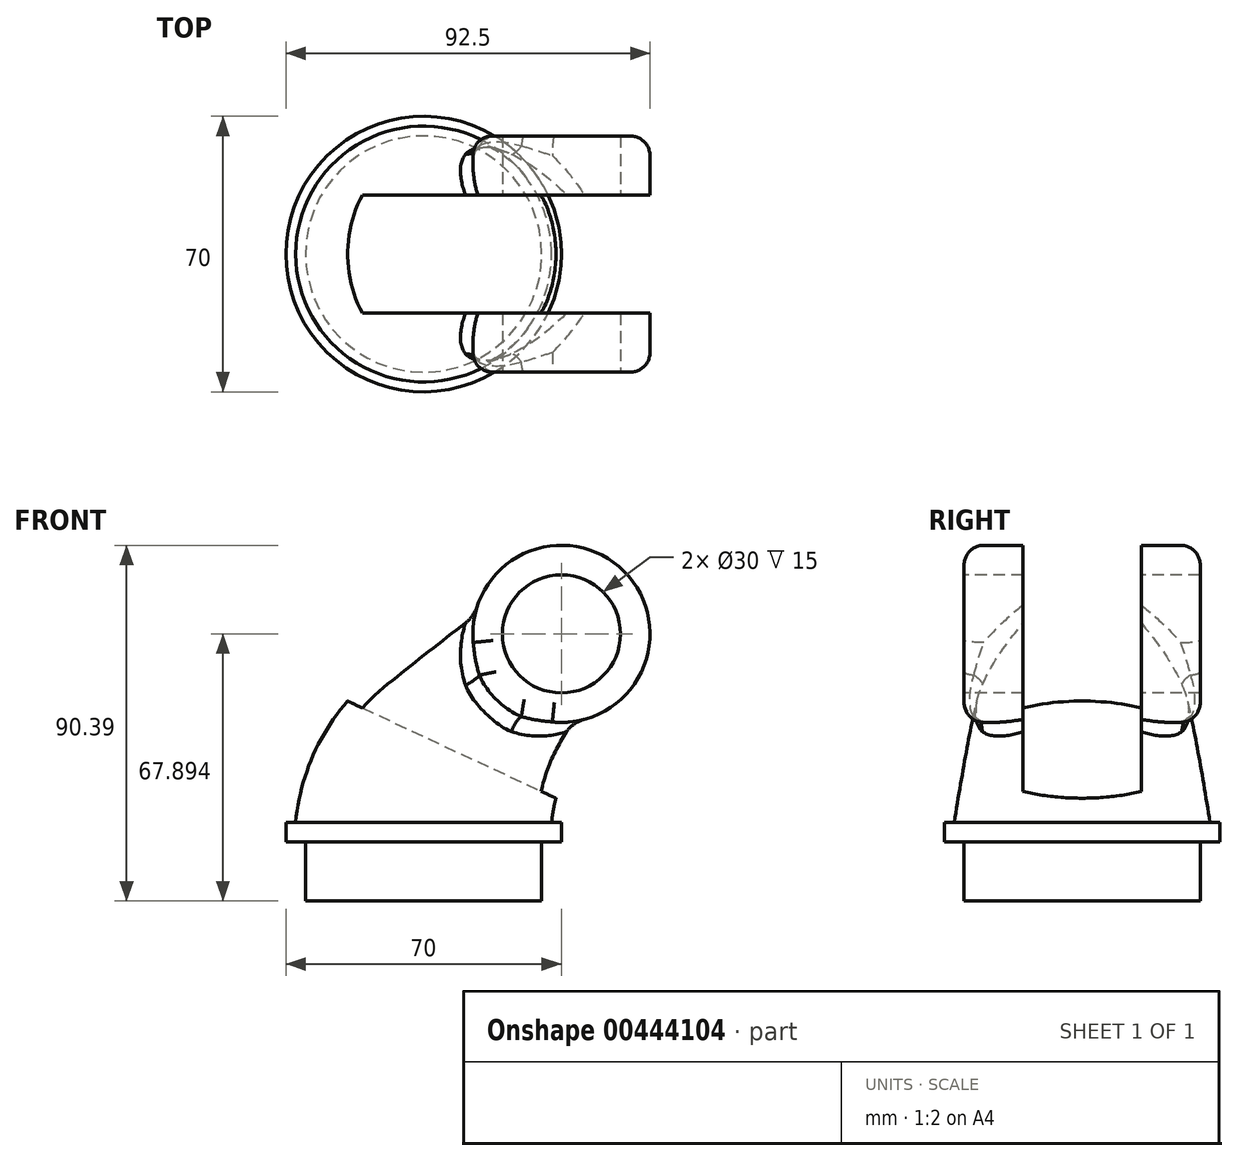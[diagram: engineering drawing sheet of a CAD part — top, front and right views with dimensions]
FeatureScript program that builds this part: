
annotation { "Feature Type Name" : "Feature", "Feature Type Description" : "" }
export const myFeature = defineFeature(function(context is Context, id is Id, definition is map)
    precondition{}
    {
        {
            var Q0;
            Q0=qCreatedBy(makeId("Top.planeOp"),FACE);
            var sketch = newSketch(context, id + "F0", { "sketchPlane" : qUnion([Q0])});
            skCircle(sketch, "E0", {"center": v(0, 0) * mm, "radius": 35 * mm});
            skSolve(sketch);
        }
        {
            var Q0;
            Q0 = qSketchRegion(id + "F0", true);
            extrude(context, id + "F1", {"entities" : qUnion([Q0]), "depth" : 5 * mm});
        }
        {
            var Q0;
            Q0=qCreatedBy(makeId("Front.planeOp"),FACE);
            var sketch = newSketch(context, id + "F2", { "sketchPlane" : qUnion([Q0])});
            skArc(sketch, "E1", {"start": v(17.6, 38.3) * mm, "mid": v(5.55, 23.37) * mm, "end": v(0, 5) * mm});
            skLineSegment(sketch, "E2", {"start": v(17.6, 38.3) * mm, "end": v(35, 52.9) * mm});
            skSolve(sketch);
        }
        {
            var Q0;
            Q0=sQuery(id+"F2.wireOp",EDGE,"E2");
            var Q1;
            Q1=sQuery(id+"F2.wireOp",VERTEX,"E2.end");
            cPlane(context, id + "F3", {"entities" : qUnion([Q0, Q1]), "cplaneType" : CPlaneType.LINE_POINT, "offset" : 25 * mm, "width" : 150 * mm, "height" : 150 * mm});
        }
        {
            var Q0;
            Q0=qCreatedBy(id+"F3.planeOp",FACE);
            var sketch = newSketch(context, id + "F4", { "sketchPlane" : qUnion([Q0])});
            skCircle(sketch, "E3", {"center": v(0, 18.02) * mm, "radius": 22.5 * mm});
            skSolve(sketch);
        }
        {
            var Q0;
            Q0=makeQuery(id+"F1.opExtrude","CAP_FACE",FACE,{"disambiguationData":[OSD([sQuery(id+"F0.wireOp",EDGE,"E0")])],"isStart":false});
            var sketch = newSketch(context, id + "F5", { "sketchPlane" : qUnion([Q0])});
            skCircle(sketch, "E4", {"center": v(0, 0) * mm, "radius": 32.5 * mm});
            skSolve(sketch);
        }
        {
            var Q0;
            Q0=qCreatedBy(makeId("Front.planeOp"),FACE);
            var sketch = newSketch(context, id + "F6", { "sketchPlane" : qUnion([Q0])});
            skArc(sketch, "E5", {"start": v(-13.25, 41.78) * mm, "mid": v(-26.5, 25.3) * mm, "end": v(-32.5, 5) * mm});
            skLineSegment(sketch, "E6", {"start": v(-13.25, 41.78) * mm, "end": v(20.54, 70.13) * mm});
            skSolve(sketch);
        }
        {
            var Q0;
            Q0=qCreatedBy(makeId("Front.planeOp"),FACE);
            var sketch = newSketch(context, id + "F7", { "sketchPlane" : qUnion([Q0])});
            skArc(sketch, "E7", {"start": v(48.46, 34.82) * mm, "mid": v(37.6, 21.45) * mm, "end": v(32.5, 5) * mm});
            skLineSegment(sketch, "E8", {"start": v(48.46, 34.82) * mm, "end": v(49.46, 35.66) * mm});
            skSolve(sketch);
        }
        {
            var Q1;
            Q1=makeQuery(id+"F5.imprint","IMPRINT",FACE,{"disambiguationData":[TD([[makeQuery(id+"F5.imprint","IMPRINT",EDGE,{"derivedFrom":sQuery(id+"F5.wireOp",EDGE,"E4")}),1.0]])]});
            var Q2;
            Q2=makeQuery(id+"F4.imprint","IMPRINT",FACE,{"disambiguationData":[TD([[makeQuery(id+"F4.imprint","IMPRINT",EDGE,{"derivedFrom":sQuery(id+"F4.wireOp",EDGE,"E3")}),1.0]])]});
            var Q3;
            Q3 = qConstructionFilter(qBodyType(qCreatedBy(id + "F7" ,EDGE), BodyType.WIRE), ConstructionObject.NO);
            var Q4;
            Q4 = qConstructionFilter(qBodyType(qCreatedBy(id + "F6" ,EDGE), BodyType.WIRE), ConstructionObject.NO);
            loft(context, id + "F8", {"operationType" : NewBodyOperationType.ADD, "addGuides" : true, "sheetProfilesArray" : [{ "sheetProfileEntities" : qUnion([Q1]) }, { "sheetProfileEntities" : qUnion([Q2]) }], "guidesArray" : [{ "guideEntities" : qUnion([Q3]), "guideDerivativeType" : LoftGuideDerivativeType.DEFAULT, "guideDerivativeMagnitude" : 1 }, { "guideEntities" : qUnion([Q4]), "guideDerivativeType" : LoftGuideDerivativeType.DEFAULT, "guideDerivativeMagnitude" : 1 }]});
        }
        {
            var Q0;
            Q0=qCreatedBy(makeId("Front.planeOp"),FACE);
            var sketch = newSketch(context, id + "F9", { "sketchPlane" : qUnion([Q0])});
            skCircle(sketch, "E9", {"center": v(35, 52.9) * mm, "radius": 22.5 * mm});
            skSolve(sketch);
        }
        {
            var Q0;
            Q0 = qSketchRegion(id + "F9", true);
            extrude(context, id + "F10", {"entities" : qUnion([Q0]), "operationType" : NewBodyOperationType.ADD, "endBound" : BoundingType.SYMMETRIC, "depth" : 60 * mm});
        }
        {
            var Q0;
            Q0=makeQuery(id+"F10.boolean.opBoolean","INTERSECT",EDGE,{"disambiguationData":[OD(1.0)],"derivedFrom":[makeQuery(id+"F8.opLoft","SWEPT_FACE",FACE,{"disambiguationData":[OSD([sQuery(id+"F4.wireOp",EDGE,"E3"),sQuery(id+"F5.wireOp",EDGE,"E4"),sQuery(id+"F6.wireOp",VERTEX,"E6.start"),sQuery(id+"F6.wireOp",EDGE,"E5"),sQuery(id+"F6.wireOp",EDGE,"E6"),sQuery(id+"F7.wireOp",VERTEX,"E8.start"),sQuery(id+"F7.wireOp",EDGE,"E7"),sQuery(id+"F7.wireOp",EDGE,"E8")])]}),makeQuery(id+"F10.opExtrude","SWEPT_FACE",FACE,{"disambiguationData":[OSD([sQuery(id+"F9.wireOp",EDGE,"E9")])]})]});
            var Q1;
            Q1=makeQuery(id+"F10.boolean.opBoolean","INTERSECT",EDGE,{"disambiguationData":[OD(0.0)],"derivedFrom":[makeQuery(id+"F8.opLoft","SWEPT_FACE",FACE,{"disambiguationData":[OSD([sQuery(id+"F4.wireOp",EDGE,"E3"),sQuery(id+"F5.wireOp",EDGE,"E4"),sQuery(id+"F6.wireOp",VERTEX,"E6.start"),sQuery(id+"F6.wireOp",EDGE,"E5"),sQuery(id+"F6.wireOp",EDGE,"E6"),sQuery(id+"F7.wireOp",VERTEX,"E8.start"),sQuery(id+"F7.wireOp",EDGE,"E7"),sQuery(id+"F7.wireOp",EDGE,"E8")])]}),makeQuery(id+"F10.opExtrude","SWEPT_FACE",FACE,{"disambiguationData":[OSD([sQuery(id+"F9.wireOp",EDGE,"E9")])]})]});
            fillet(context, id + "F11", {"entities" : qUnion([Q0, Q1]), "radius" : 5 * mm, "tangentPropagation" : true, "allowEdgeOverflow" : false});
        }
        {
            var Q0;
            Q0=makeQuery(id+"F10.opExtrude","CAP_EDGE",EDGE,{"disambiguationData":[OSD([sQuery(id+"F9.wireOp",EDGE,"E9")])],"isStart":true});
            var Q1;
            Q1=makeQuery(id+"F10.opExtrude","CAP_FACE",FACE,{"disambiguationData":[OSD([sQuery(id+"F9.wireOp",EDGE,"E9")])],"isStart":false});
            fillet(context, id + "F12", {"entities" : qUnion([Q0, Q1]), "radius" : 5 * mm, "tangentPropagation" : true, "allowEdgeOverflow" : false});
        }
        {
            var Q0;
            Q0=makeQuery(id+"F10.opExtrude","CAP_FACE",FACE,{"disambiguationData":[OSD([sQuery(id+"F9.wireOp",EDGE,"E9")])],"isStart":false});
            var sketch = newSketch(context, id + "F13", { "sketchPlane" : qUnion([Q0])});
            skCircle(sketch, "E10", {"center": v(35, 52.9) * mm, "radius": 15 * mm});
            skSolve(sketch);
        }
        {
            var Q0;
            Q0 = qSketchRegion(id + "F13", true);
            extrude(context, id + "F14", {"entities" : qUnion([Q0]), "operationType" : NewBodyOperationType.REMOVE, "endBound" : BoundingType.THROUGH_ALL, "oppositeDirection" : true, "depth" : 25 * mm});
        }
        {
            var Q0;
            Q0=qCreatedBy(makeId("Front.planeOp"),FACE);
            var sketch = newSketch(context, id + "F15", { "sketchPlane" : qUnion([Q0])});
            skLineSegment(sketch, "E11", {"start": v(-104.18, 75.4) * mm, "end": v(57.5, 0) * mm});
            skLineSegment(sketch, "E12", {"start": v(57.5, 75.4) * mm, "end": v(57.5, 0) * mm});
            skLineSegment(sketch, "E13", {"start": v(-104.18, 75.4) * mm, "end": v(57.5, 75.4) * mm});
            skSolve(sketch);
        }
        {
            var Q0;
            Q0 = qSketchRegion(id + "F15", true);
            extrude(context, id + "F16", {"entities" : qUnion([Q0]), "operationType" : NewBodyOperationType.REMOVE, "endBound" : BoundingType.SYMMETRIC, "oppositeDirection" : true, "depth" : 30 * mm});
        }
        {
            var Q0;
            Q0=qCreatedBy(makeId("Front.planeOp"),FACE);
            var sketch = newSketch(context, id + "F17", { "sketchPlane" : qUnion([Q0])});
            skLineSegment(sketch, "E14.bottom", {"start": v(0, 0) * mm, "end": v(-30, 0) * mm});
            skLineSegment(sketch, "E14.top", {"start": v(0, -15) * mm, "end": v(-30, -15) * mm});
            skLineSegment(sketch, "E14.left", {"start": v(0, 0) * mm, "end": v(0, -15) * mm});
            skLineSegment(sketch, "E14.right", {"start": v(-30, 0) * mm, "end": v(-30, -15) * mm});
            skSolve(sketch);
        }
        {
            var Q0;
            Q0=makeQuery(id+"F17.imprint","IMPRINT",FACE,{"disambiguationData":[TD([[makeQuery(id+"F17.imprint","IMPRINT",EDGE,{"derivedFrom":sQuery(id+"F17.wireOp",EDGE,"E14.bottom")}),1.0]])]});
            var Q1;
            Q1=sQuery(id+"F17.wireOp",EDGE,"E14.left");
            revolve(context, id + "F18", {"operationType" : NewBodyOperationType.ADD, "entities" : qUnion([Q0]), "axis" : qUnion([Q1]), "revolveType" : RevolveType.FULL});
        }
    });
